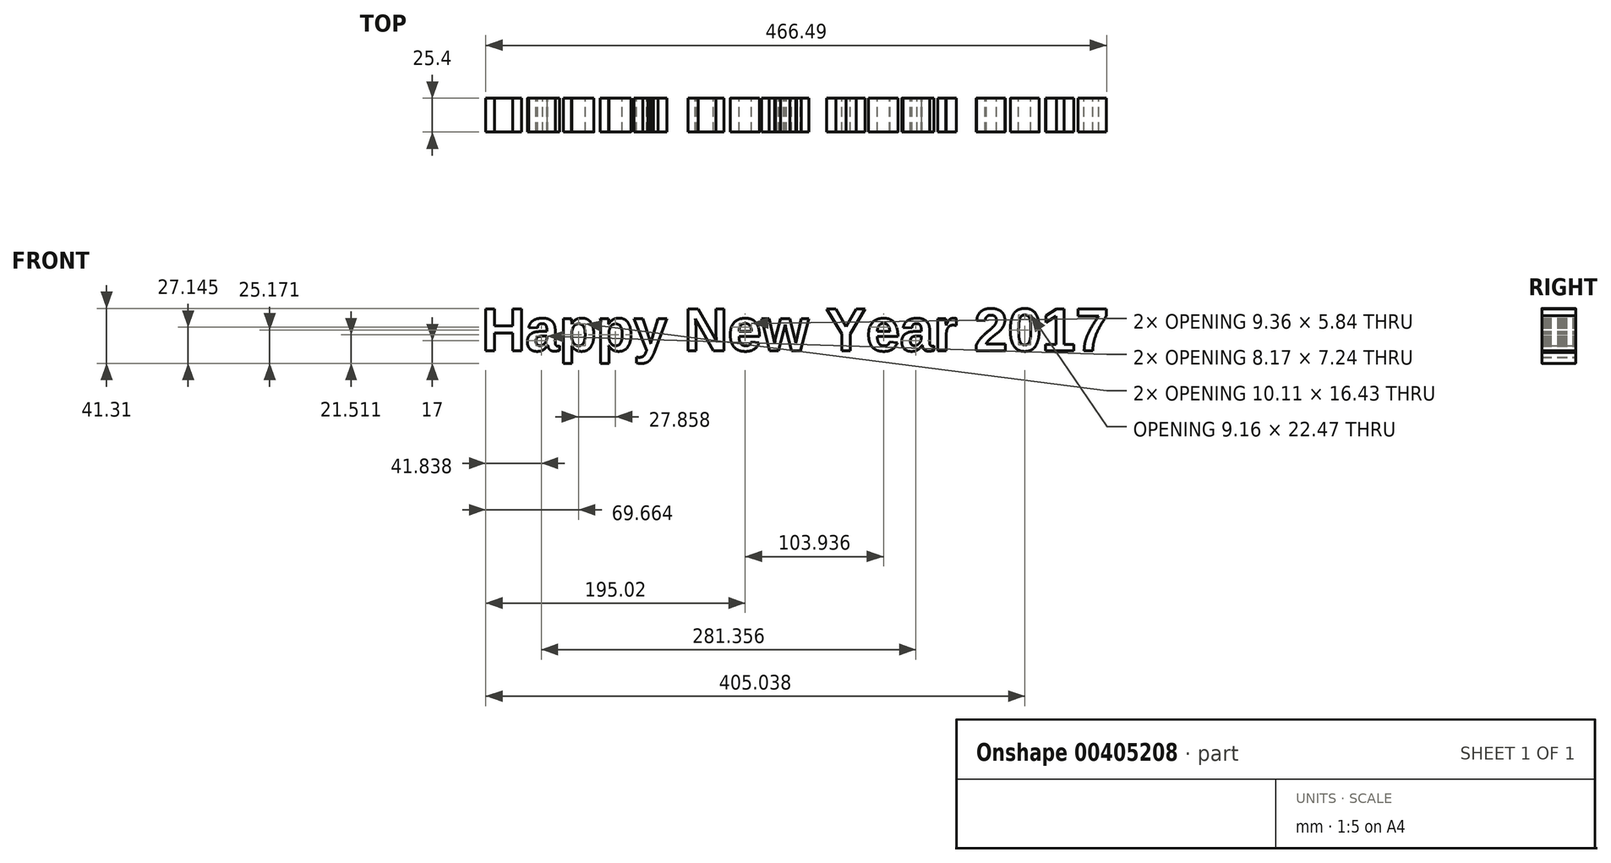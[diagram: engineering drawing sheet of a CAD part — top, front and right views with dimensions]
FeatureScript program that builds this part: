
annotation { "Feature Type Name" : "Feature", "Feature Type Description" : "" }
export const myFeature = defineFeature(function(context is Context, id is Id, definition is map)
    precondition{}
    {
        {
            var Q0;
            Q0=qCreatedBy(makeId("Front.planeOp"),FACE);
            var sketch = newSketch(context, id + "F0", { "sketchPlane" : qUnion([Q0])});
            skText(sketch, "E0", { "text": "Happy New Year 2017", "fontName": "Arimo-Bold.ttf"});
            const initialGuessF0  = {"E0": [-0.14688, 0, 1, 0, 0.03284]};
            skSetInitialGuess(sketch, initialGuessF0);
            skSolve(sketch);
        }
        {
            var Q0;
            Q0 = qSketchRegion(id + "F0", true);
            extrude(context, id + "F1", {"entities" : qUnion([Q0]), "depth" : 25.4 * mm});
        }
    });
